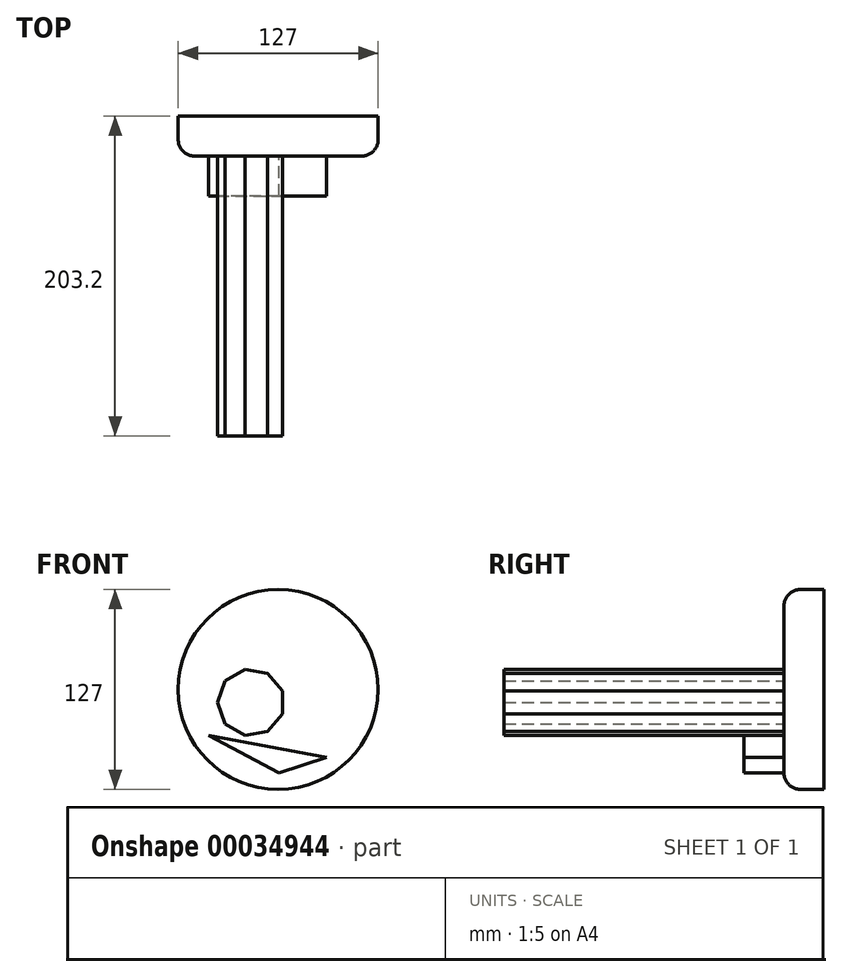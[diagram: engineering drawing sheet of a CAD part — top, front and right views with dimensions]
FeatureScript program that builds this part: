
annotation { "Feature Type Name" : "Feature", "Feature Type Description" : "" }
export const myFeature = defineFeature(function(context is Context, id is Id, definition is map)
    precondition{}
    {
        {
            var Q0;
            Q0=qCreatedBy(makeId("Front.planeOp"),FACE);
            var sketch = newSketch(context, id + "F0", { "sketchPlane" : qUnion([Q0])});
            skCircle(sketch, "E0", {"center": v(17.3, 8.2) * mm, "radius": 63.5 * mm});
            skSolve(sketch);
        }
        {
            var Q0;
            Q0 = qSketchRegion(id + "F0", true);
            extrude(context, id + "F1", {"entities" : qUnion([Q0]), "depth" : 25.4 * mm});
        }
        {
            var Q0;
            Q0=makeQuery(id+"F1.opExtrude","CAP_EDGE",EDGE,{"disambiguationData":[OSD([sQuery(id+"F0.wireOp",EDGE,"E0")])],"isStart":false});
            fillet(context, id + "F2", {"entities" : qUnion([Q0]), "radius" : 10.54 * mm, "tangentPropagation" : true, "allowEdgeOverflow" : false});
        }
        {
            var Q0;
            Q0=makeQuery(id+"F1.opExtrude","CAP_FACE",FACE,{"disambiguationData":[OSD([sQuery(id+"F0.wireOp",EDGE,"E0")])],"isStart":false});
            var sketch = newSketch(context, id + "F3", { "sketchPlane" : qUnion([Q0])});
            skLineSegment(sketch, "E1", {"start": v(48, -34.94) * mm, "end": v(18, -44.75) * mm});
            skLineSegment(sketch, "E2", {"start": v(18, -44.75) * mm, "end": v(-26.9, -20.97) * mm});
            skLineSegment(sketch, "E3", {"start": v(-26.9, -20.97) * mm, "end": v(48, -34.94) * mm});
            skSolve(sketch);
        }
        {
            var Q0;
            Q0=makeQuery(id+"F3.imprint","IMPRINT",FACE,{"disambiguationData":[TD([[makeQuery(id+"F3.imprint","IMPRINT",EDGE,{"derivedFrom":sQuery(id+"F3.wireOp",EDGE,"E1")}),-1.0]])]});
            extrude(context, id + "F4", {"entities" : qUnion([Q0]), "operationType" : NewBodyOperationType.ADD, "depth" : 25.4 * mm});
        }
        {
            var Q0;
            Q0=makeQuery(id+"F4.boolean.opBoolean","SPLIT",FACE,{"disambiguationData":[OD(2.0)],"derivedFrom":makeQuery(id+"F1.opExtrude","CAP_FACE",FACE,{"disambiguationData":[OSD([sQuery(id+"F0.wireOp",EDGE,"E0")])],"isStart":false})});
            var sketch = newSketch(context, id + "F5", { "sketchPlane" : qUnion([Q0])});
            skCircle(sketch, "E4.cCircle", {"center": v(0, 0) * mm, "radius": 20.03 * mm, "construction": true});
            skLineSegment(sketch, "E4.0", {"start": v(20.03, 7.3) * mm, "end": v(20.03, -7.3) * mm});
            skLineSegment(sketch, "E4.1", {"start": v(20.03, -7.3) * mm, "end": v(10.66, -18.46) * mm});
            skLineSegment(sketch, "E4.2", {"start": v(10.66, -18.46) * mm, "end": v(-3.7, -21) * mm});
            skLineSegment(sketch, "E4.3", {"start": v(-3.7, -21) * mm, "end": v(-16.33, -13.7) * mm});
            skLineSegment(sketch, "E4.4", {"start": v(-16.33, -13.7) * mm, "end": v(-21.32, 0) * mm});
            skLineSegment(sketch, "E4.5", {"start": v(-21.32, 0) * mm, "end": v(-16.33, 13.7) * mm});
            skLineSegment(sketch, "E4.6", {"start": v(-16.33, 13.7) * mm, "end": v(-3.7, 21) * mm});
            skLineSegment(sketch, "E4.7", {"start": v(-3.7, 21) * mm, "end": v(10.66, 18.46) * mm});
            skLineSegment(sketch, "E4.8", {"start": v(10.66, 18.46) * mm, "end": v(20.03, 7.3) * mm});
            skPoint(sketch, "E4.0.midPoint", {"position": v(20.03, 0) * mm});
            skSolve(sketch);
        }
        {
            var Q0;
            Q0 = qSketchRegion(id + "F5", true);
            extrude(context, id + "F6", {"entities" : qUnion([Q0]), "operationType" : NewBodyOperationType.ADD, "depth" : 177.8 * mm});
        }
    });
